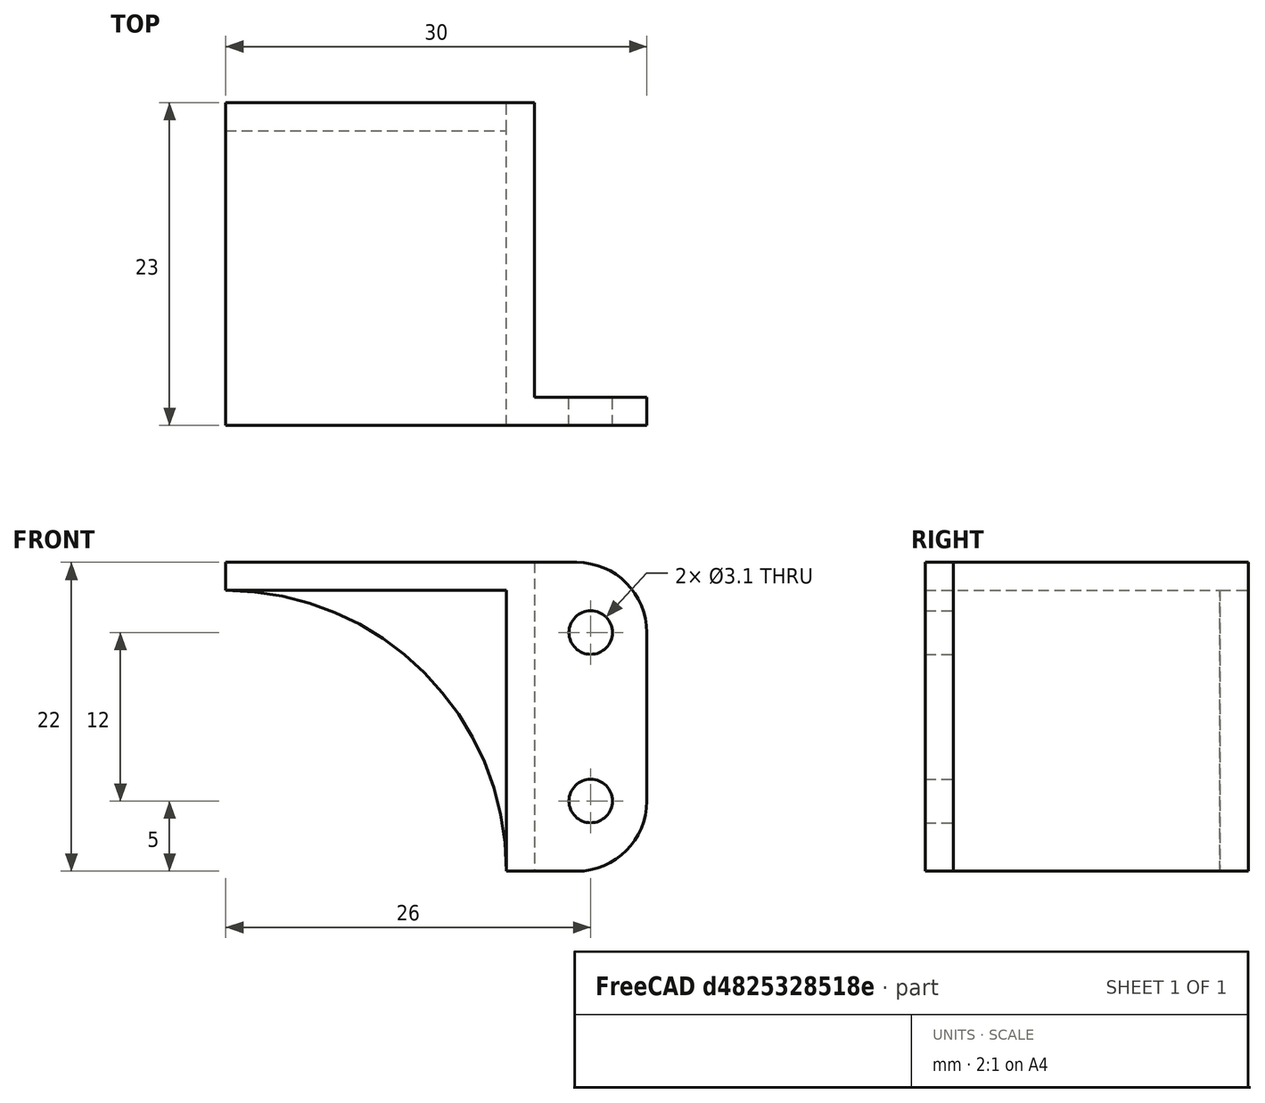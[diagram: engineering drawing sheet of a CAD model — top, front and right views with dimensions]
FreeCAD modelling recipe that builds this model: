
FCSTD DOCUMENT  (FreeCAD 0.17R13541 (Git))
Label: sujetador-right
License: All rights reserved
LicenseURL: http://en.wikipedia.org/wiki/All_rights_reserved
objects: Part::Cut×5, Part::Box×4, Part::Cylinder×3, Part::Fillet×2, Part::MultiFuse×1
note: 15 computed .brp shape members not serialized (recipe doc carries the construction recipe); baked Part::Feature solids carry a one-line shape summary decoded from their .brp

FEATURE [Part::Box] Box  label="Cubo"
  AttacherType = Attacher::AttachEngine3D
  Height = 22
  Length = 22
  Width = 23
FEATURE [Part::Box] Box001  label="Cubo001"
  AttacherType = Attacher::AttachEngine3D
  Height = 20
  Length = 20
  Width = 21
FEATURE [Part::Box] Box002  label="Cubo002"
  AttacherType = Attacher::AttachEngine3D
  Height = 30
  Length = 30
  Width = 2
FEATURE [Part::Cylinder] Cylinder  label="Cilindro"
  Angle = 360
  AttacherType = Attacher::AttachEngine3D
  Height = 10
  Placement = pos=(26,-2,5) rot=(-1,0,0;1.5708rad)
  Radius = 1.55
FEATURE [Part::Cylinder] Cylinder001  label="Cilindro001"
  Angle = 360
  AttacherType = Attacher::AttachEngine3D
  Height = 25
  Placement = pos=(0,0,0) rot=(-1,0,0;1.5708rad)
  Radius = 20
FEATURE [Part::Cylinder] Cylinder002  label="Cilindro002"
  Angle = 360
  AttacherType = Attacher::AttachEngine3D
  Height = 10
  Placement = pos=(26,-2,17) rot=(-1,0,0;1.5708rad)
  Radius = 1.55
FEATURE [Part::MultiFuse] Fusion
  Refine = true
  Shapes = -> [Box002,Box]
FEATURE [Part::Cut] Cut
  Base = -> Fusion
  Refine = true
  Tool = -> Box001
FEATURE [Part::Box] Box003  label="Cubo003"
  AttacherType = Attacher::AttachEngine3D
  Height = 10
  Length = 35
  Placement = pos=(0,0,22) rot=(0,0,1;0rad)
  Width = 9
FEATURE [Part::Cut] Cut001
  Base = -> Cut
  Refine = true
  Tool = -> Box003
FEATURE [Part::Cut] Cut002
  Base = -> Cut001
  Refine = true
  Tool = -> Cylinder002
FEATURE [Part::Cut] Cut003
  Base = -> Cut002
  Refine = true
  Tool = -> Cylinder001
FEATURE [Part::Cut] Cut004
  Base = -> Cut003
  Refine = true
  Tool = -> Cylinder
FEATURE [Part::Fillet] Fillet
  Base = -> Cut004
  Edges = 1 edges r=5: [Edge25]
FEATURE [Part::Fillet] Fillet001
  Base = -> Fillet
  Edges = 1 edges r=5: [Edge20]
